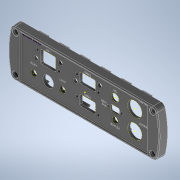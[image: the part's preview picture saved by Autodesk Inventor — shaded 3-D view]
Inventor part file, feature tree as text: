
AUTODESK INVENTOR PART (.ipt)
format: ipt  version: 2021 (Build 250183000, 183)  size: 1,206,272 bytes
history: native  units: mm
features: extrude x13, sketch x13, fillet x5, other x4, plane x3, mirror x1, hole x1, chamfer x1, reference x1
ambient origin geometry x8: Origin, YZ Plane, XZ Plane, XY Plane, X Axis, Y Axis, Z Axis, Center Point
bodies: Solid1 (feature_tree)
feature tree (42):
  other  "1009799_3D"
  extrude  "Extrusion1"  Depth=4.85mm
  fillet  "Fillet1"  Radius=27.0mm
  plane  "Work Plane1"
  extrude  "Extrusion2"  Depth=3.5mm
  plane  "Work Plane3"
  mirror  "Mirror2"
  extrude  "Extrusion7"  Depth=3.3mm
  extrude  "Extrusion8"  Depth=5.0mm
  extrude  "Extrusion9"  Depth=11.55mm
  extrude  "Extrusion10"  TaperAngle=0.0deg  [1 undecoded]
  extrude  "Extrusion11"  Depth=8.225mm
  fillet  "Fillet3"  Radius=6.9mm
  extrude  "Extrusion12"  Depth=1.35mm
  fillet  "Fillet4"  Radius=9.408852mm
  extrude  "Extrusion13"  Depth=1.275mm
  extrude  "Extrusion14"  Depth=3.225mm
  hole  "Hole1"  [1 undecoded]
  extrude  "Extrusion16"  Depth=1.0mm
  fillet  "Fillet5"  Radius=11.5mm
  extrude  "Extrusion18"  Depth=1.0mm
  fillet  "Fillet6"  Radius=7.0mm
  extrude  "Extrusion19"  Depth=1.0mm
  chamfer  "Chamfer6"  Distance=7.0mm
  sketch  "Sketch29"  dims[d82=0.05mm d83=0.05mm d85=11.5mm d86=4.85mm d87=4.85mm d88=27.0mm d90=3.3mm d91=3.3mm d92=24.0mm d93=16.55mm d94=14.55mm d95=9.0mm d96=4.5mm d97=3.725mm d98=5.225mm d100=0.05mm d101=3.725mm d102=5.225mm d104=7.0mm d105=7.0mm d106=7.0mm d107=7.0mm d108=4.5mm d109=4.5mm d112=9.125mm d113=9.125mm d114=30.0mm d115=44.0mm d116=10.0mm d117=0.0mm d118=11.55mm d119=5.775mm d120=16.0mm d121=16.0mm d122=6.5mm d123=6.5mm d124=12.2mm d125=16.0mm d126=16.0mm d128=16.55mm d129=21.725mm d130=30.0mm d132=10.075mm d134=16.2mm d135=8.13mm d136=0.0mm d137=22.0mm d138=0.0mm d139=0.0mm d141=6.35mm d142=0.0mm d143=0.0mm d144=10.0mm d145=0.0mm d147=1.275mm d148=1.275mm d149=13.908852mm d150=0.7125mm d151=11.55mm d152=5.775mm d154=11.55mm d155=9.75mm d156=6.75mm d157=3.0mm d158=7.5mm d159=0.0mm d160=0.0mm d161=1.25mm d164=16.0mm d165=4.875mm d166=9.75mm d167=22.0mm d168=11.0mm d169=1.5mm d170=0.0mm d171=2.0mm d172=12.4mm d173=0.0mm d174=0.0mm d175=1.5mm d176=0.0mm d177=6.5mm d178=0.0mm d179=0.0mm d199=3.25mm d200=6.0mm d201=6.25mm d202=2.0mm d203=90.0deg d204=8.0mm d205=20.594885mm d206=13.0mm d207=10.0mm d208=0.0mm d209=2.0mm d214=20.0mm d215=0.2mm d216=0.0mm d217=0.0mm d218=3.0mm d219=20.0mm d220=0.0mm d221=7.877954mm d222=0.2mm d223=2.0mm d224=45.0deg d225=1.5mm d226=0.8mm d227=0.8mm d228=1.5mm d229=0.85mm d230=6.75mm d231=4.75mm d232=5.0mm d233=2.75mm d234=3.5mm d235=1.5mm d236=5.0mm d237=1.0mm d238=1.0mm d239=4.75mm d240=1.0mm d241=5.5mm d242=4.5mm d243=4.5mm d244=3.5mm d245=3.5mm]
  plane  "Work Plane2"
  sketch  "Sketch10"  dims[d0=4.85mm d1=4.85mm d2=27.0mm]
  sketch  "Sketch11"  dims[d3=9.0mm d4=3.5mm]
  sketch  "Sketch12"  dims[d6=3.3mm d7=3.3mm]
  sketch  "Sketch13"  dims[d8=24.0mm d9=5.0mm]
  sketch  "Sketch14"  dims[d11=16.55mm d12=11.55mm]
  sketch  "Sketch15"  dims[d14=17.0mm d15=0.0mm d16=0.0mm]
  sketch  "Sketch16"  dims[d17=6.35mm d20=8.225mm d21=6.9mm]
  sketch  "Sketch17"  dims[d22=1.85mm d23=1.35mm]
  reference  "Reference1"
  sketch  "Sketch23"  dims[d26=-1.5mm d27=10.0mm d28=0.0mm d65=9.408852mm]
  sketch  "Sketch24"  dims[d66=4.85mm d67=4.85mm d68=27.0mm d69=9.0mm d70=3.3mm d71=3.3mm d72=24.0mm d73=17.55mm d74=11.55mm d75=6.35mm d76=1.85mm d77=1.275mm]
  sketch  "Sketch26"  dims[d78=3.725mm d79=3.225mm]
  sketch  "Sketch27"  dims[d80=4.725mm d81=5.225mm]
  other  "Image1"
  other  "<userpath>\Google Drive\Unicorn 2020\CAD\Assembly.iam"
  other  "Assembly.iam"
note: 2 required parameter values undecoded (feature->parameter linkage not recoverable at this tier; creation-order binding heuristic only, values carry confidence <= 0.55)
